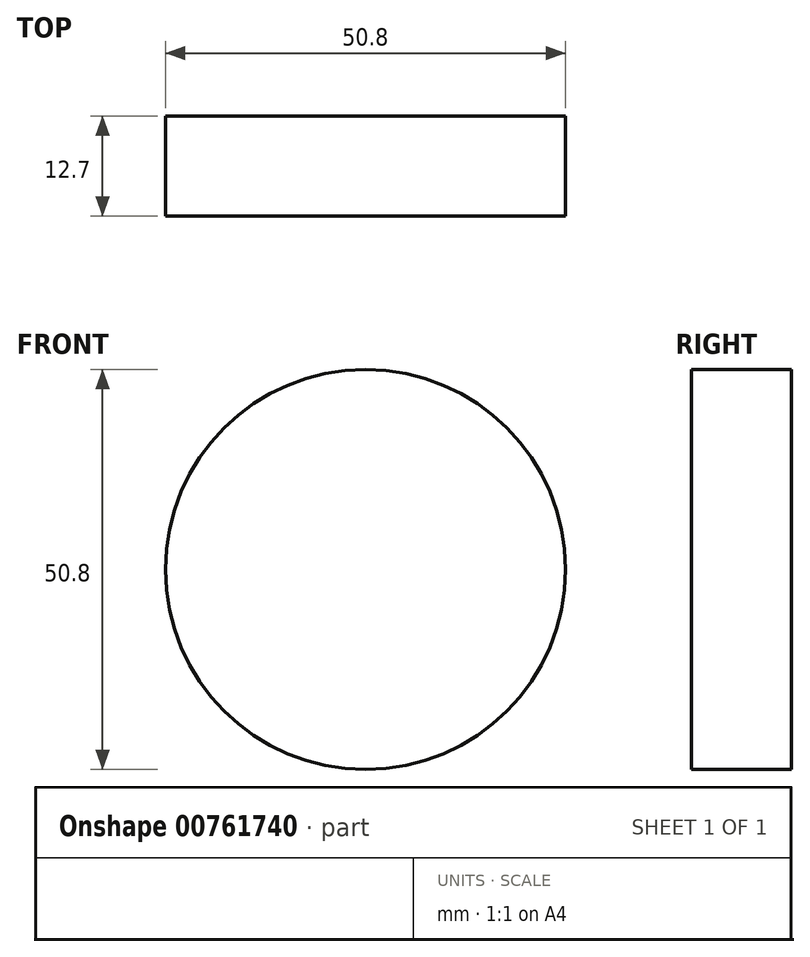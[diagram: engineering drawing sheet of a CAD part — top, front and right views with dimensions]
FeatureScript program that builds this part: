
annotation { "Feature Type Name" : "Feature", "Feature Type Description" : "" }
export const myFeature = defineFeature(function(context is Context, id is Id, definition is map)
    precondition{}
    {
        {
            var Q0;
            Q0=qCreatedBy(makeId("Front.planeOp"),FACE);
            var sketch = newSketch(context, id + "F0", { "sketchPlane" : qUnion([Q0])});
            skCircle(sketch, "E0", {"center": v(-43.97, 41.66) * mm, "radius": 25.4 * mm});
            skSolve(sketch);
        }
        {
            var Q0;
            Q0 = qSketchRegion(id + "F0", true);
            extrude(context, id + "F1", {"entities" : qUnion([Q0]), "depth" : 12.7 * mm, "offsetDistance" : 25.4 * mm});
        }
    });
